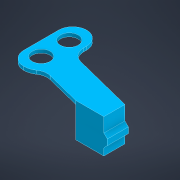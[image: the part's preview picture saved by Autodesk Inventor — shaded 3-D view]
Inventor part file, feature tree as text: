
AUTODESK INVENTOR PART (.ipt)
format: ipt  version: 2022 (Build 260153000, 153)  size: 430,080 bytes
history: native  units: in
note: dims shown in document units (in); Inventor stores cm internally (conversion verified against a paired STEP export)
features: extrude x7, sketch x7, projected_geometry x4, chamfer x2, fillet x1
ambient origin geometry x8: Origin, YZ Plane, XZ Plane, XY Plane, X Axis, Y Axis, Z Axis, Center Point
bodies: Solid1 (feature_tree)
feature tree (21):
  extrude  "Extrusion1"  Depth=0.722in
  extrude  "Extrusion2"  Depth=1.0in
  extrude  "Extrusion3"  Depth=0.375in TaperAngle=0.0deg
  extrude  "Extrusion4"  Depth=3.0in
  fillet  "Fillet1"  Radius=1.75in
  extrude  "Extrusion5"  Depth=0.64in
  chamfer  "Chamfer1"  Distance=0.125in
  extrude  "Extrusion6"  Depth=0.125in TaperAngle=0.0deg
  extrude  "Extrusion7"  Depth=0.125in TaperAngle=45.0deg
  chamfer  "Chamfer2"  Distance=0.156in
  sketch  "Sketch1"  dims[d0=0.125in d1=0.722in]
  sketch  "Sketch2"  dims[d2=0.63in d3=0.0in d4=1.0in]
  projected_geometry  "Projected Loop1"
  sketch  "Sketch3"  dims[d5=0.125in d6=0.0in d7=0.375in d8=0.0in]
  sketch  "Sketch4"  dims[d9=0.5in d10=3.0in d11=1.75in]
  sketch  "Sketch5"  dims[d12=1.0in d13=0.64in]
  sketch  "Sketch6"  dims[d14=0.504in d15=0.125in d16=0.0in]
  projected_geometry  "Projected Loop2"
  projected_geometry  "Projected Loop3"
  sketch  "Sketch7"  dims[d17=0.5in d18=0.125in d19=0.0in d20=0.125in d21=0.125in d22=45.0deg d23=0.156in d24=0.08in d25=0.0in d26=0.5in d27=0.0in d28=0.125in d29=0.0in d30=0.125in d31=0.125in d32=45.0deg]
  projected_geometry  "Projected Loop4"
